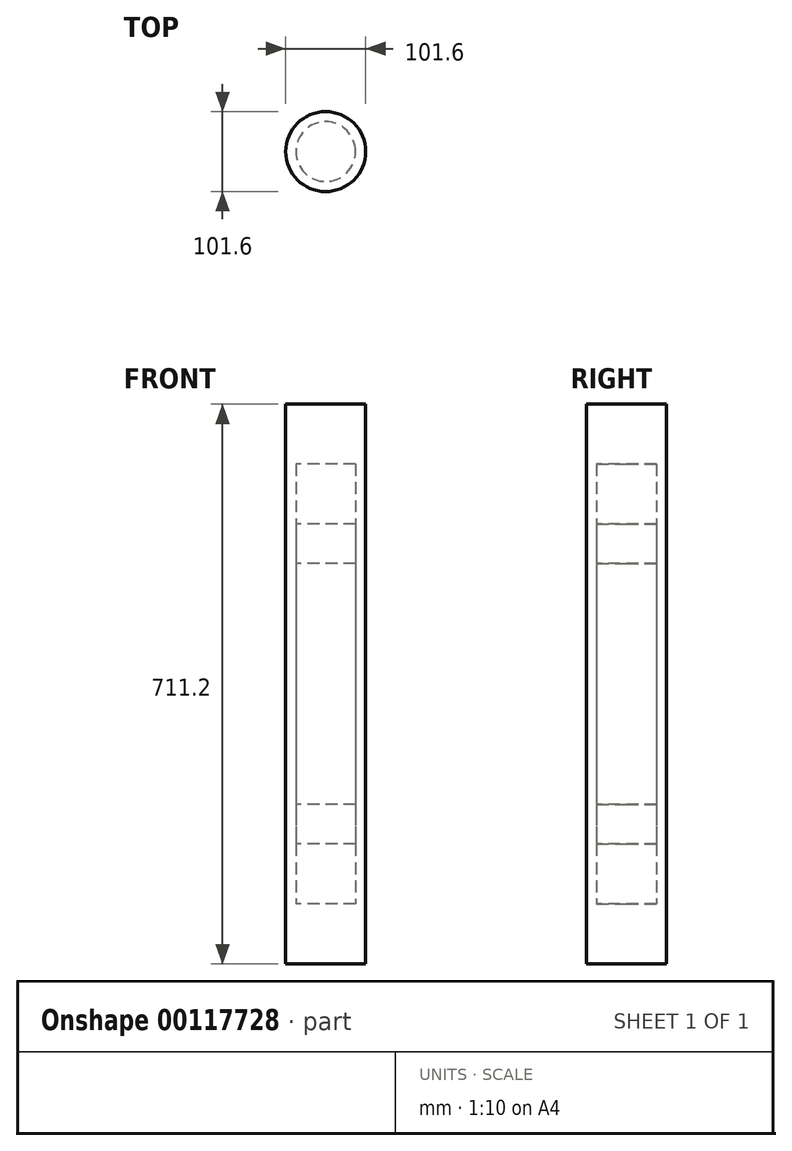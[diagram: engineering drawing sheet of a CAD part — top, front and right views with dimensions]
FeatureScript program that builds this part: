
annotation { "Feature Type Name" : "Feature", "Feature Type Description" : "" }
export const myFeature = defineFeature(function(context is Context, id is Id, definition is map)
    precondition{}
    {
        {
            var Q0;
            Q0=qCreatedBy(makeId("Top.planeOp"),FACE);
            var sketch = newSketch(context, id + "F0", { "sketchPlane" : qUnion([Q0])});
            skCircle(sketch, "E0", {"center": v(0, 0) * mm, "radius": 37.97 * mm});
            skSolve(sketch);
        }
        {
            var Q0;
            Q0 = qSketchRegion(id + "F0", true);
            extrude(context, id + "F1", {"entities" : qUnion([Q0]), "endBound" : BoundingType.SYMMETRIC, "depth" : 306.07 * mm});
        }
        {
            var Q0;
            Q0=makeQuery(id+"F0.imprint","IMPRINT",FACE,{"disambiguationData":[TD([[makeQuery(id+"F0.imprint","IMPRINT",EDGE,{"derivedFrom":sQuery(id+"F0.wireOp",EDGE,"E0")}),1.0]])]});
            extrude(context, id + "F2", {"entities" : qUnion([Q0]), "endBound" : BoundingType.SYMMETRIC, "depth" : 406.4 * mm});
        }
        {
            var Q0;
            Q0=makeQuery(id+"F0.imprint","IMPRINT",FACE,{"disambiguationData":[TD([[makeQuery(id+"F0.imprint","IMPRINT",EDGE,{"derivedFrom":sQuery(id+"F0.wireOp",EDGE,"E0")}),1.0]])]});
            extrude(context, id + "F3", {"entities" : qUnion([Q0]), "endBound" : BoundingType.SYMMETRIC, "depth" : 558.8 * mm});
        }
        {
            var Q0;
            Q0=qCreatedBy(makeId("Top.planeOp"),FACE);
            var sketch = newSketch(context, id + "F4", { "sketchPlane" : qUnion([Q0])});
            skCircle(sketch, "E1", {"center": v(0, 0) * mm, "radius": 50.8 * mm});
            skSolve(sketch);
        }
        {
            var Q0;
            Q0 = qSketchRegion(id + "F4", true);
            extrude(context, id + "F5", {"entities" : qUnion([Q0]), "endBound" : BoundingType.SYMMETRIC, "depth" : 711.2 * mm});
        }
    });
